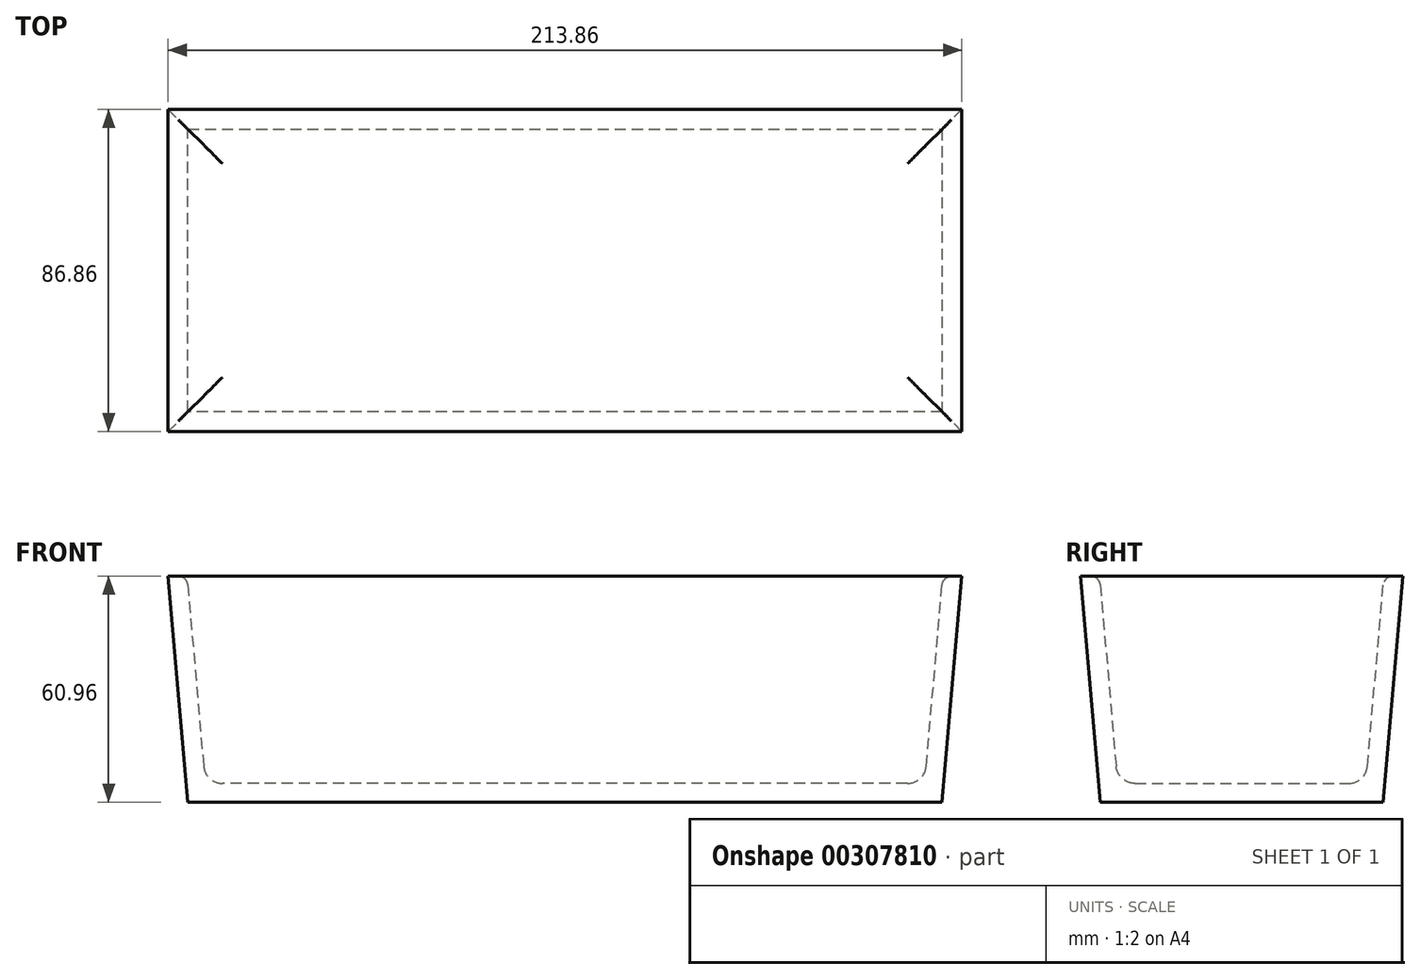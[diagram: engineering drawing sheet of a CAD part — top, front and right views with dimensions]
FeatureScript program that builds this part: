
annotation { "Feature Type Name" : "Feature", "Feature Type Description" : "" }
export const myFeature = defineFeature(function(context is Context, id is Id, definition is map)
    precondition{}
    {
        {
            var Q0;
            Q0=qCreatedBy(makeId("Top.planeOp"),FACE);
            var sketch = newSketch(context, id + "F0", { "sketchPlane" : qUnion([Q0])});
            skLineSegment(sketch, "E0.bottom", {"start": v(101.6, 38.1) * mm, "end": v(-101.6, 38.1) * mm});
            skLineSegment(sketch, "E0.top", {"start": v(101.6, -38.1) * mm, "end": v(-101.6, -38.1) * mm});
            skLineSegment(sketch, "E0.left", {"start": v(101.6, 38.1) * mm, "end": v(101.6, -38.1) * mm});
            skLineSegment(sketch, "E0.right", {"start": v(-101.6, 38.1) * mm, "end": v(-101.6, -38.1) * mm});
            skPoint(sketch, "E0.middle", {"position": v(0, 0) * mm});
            skSolve(sketch);
        }
        {
            var Q0;
            Q0 = qSketchRegion(id + "F0", true);
            extrude(context, id + "F1", {"entities" : qUnion([Q0]), "depth" : 60.96 * mm, "hasDraft" : true, "draftAngle" : 5 * degree});
        }
        {
            var Q0;
            Q0=makeQuery(id+"F1.opExtrude","CAP_FACE",FACE,{"disambiguationData":[OSD([sQuery(id+"F0.wireOp",EDGE,"E0.bottom"),sQuery(id+"F0.wireOp",EDGE,"E0.top"),sQuery(id+"F0.wireOp",EDGE,"E0.left"),sQuery(id+"F0.wireOp",EDGE,"E0.right")])],"isStart":false});
            shell(context, id + "F2", {"entities" : qUnion([Q0]), "thickness" : 5.08 * mm});
        }
        {
            var Q0;
            {var subQ0=sQuery(id+"F0.wireOp",EDGE,"E0.bottom");Q0=makeQuery(id+"F2.opShell","OFFSET_EDGE",EDGE,{"disambiguationData":[OSD([subQ0]),TDD([makeQuery(id+"F1.opExtrude","CAP_EDGE",EDGE,{"disambiguationData":[OSD([subQ0])],"isStart":false})])]});}
            var Q1;
            {var subQ0=sQuery(id+"F0.wireOp",EDGE,"E0.right");Q1=makeQuery(id+"F2.opShell","OFFSET_EDGE",EDGE,{"disambiguationData":[OSD([subQ0]),TDD([makeQuery(id+"F1.opExtrude","CAP_EDGE",EDGE,{"disambiguationData":[OSD([subQ0])],"isStart":false})])]});}
            var Q2;
            {var subQ0=sQuery(id+"F0.wireOp",EDGE,"E0.top");Q2=makeQuery(id+"F2.opShell","OFFSET_EDGE",EDGE,{"disambiguationData":[OSD([subQ0]),TDD([makeQuery(id+"F1.opExtrude","CAP_EDGE",EDGE,{"disambiguationData":[OSD([subQ0])],"isStart":false})])]});}
            var Q3;
            {var subQ0=sQuery(id+"F0.wireOp",EDGE,"E0.left");Q3=makeQuery(id+"F2.opShell","OFFSET_EDGE",EDGE,{"disambiguationData":[OSD([subQ0]),TDD([makeQuery(id+"F1.opExtrude","CAP_EDGE",EDGE,{"disambiguationData":[OSD([subQ0])],"isStart":false})])]});}
            fillet(context, id + "F3", {"entities" : qUnion([Q0, Q1, Q2, Q3]), "radius" : 2.54 * mm, "tangentPropagation" : true, "allowEdgeOverflow" : false});
        }
        {
            var Q0;
            Q0=makeQuery(id+"F2.opShell","OFFSET_FACE",FACE,{"disambiguationData":[OSD([sQuery(id+"F0.wireOp",EDGE,"E0.bottom"),sQuery(id+"F0.wireOp",EDGE,"E0.top"),sQuery(id+"F0.wireOp",EDGE,"E0.left"),sQuery(id+"F0.wireOp",EDGE,"E0.right")])]});
            fillet(context, id + "F4", {"entities" : qUnion([Q0]), "radius" : 5.08 * mm, "tangentPropagation" : true, "allowEdgeOverflow" : false});
        }
    });
